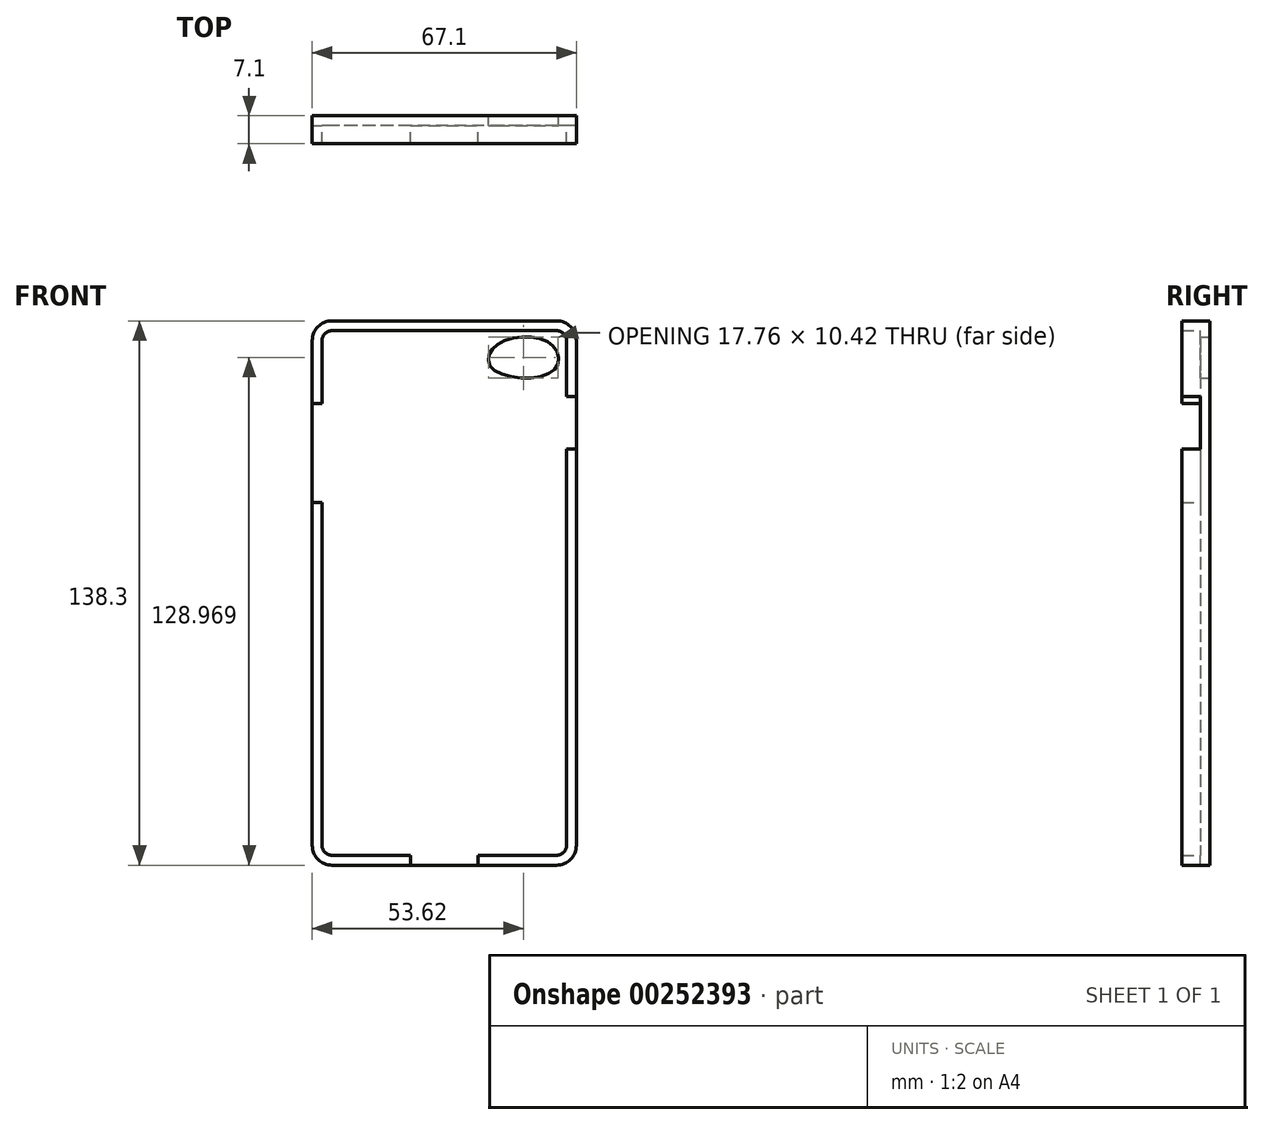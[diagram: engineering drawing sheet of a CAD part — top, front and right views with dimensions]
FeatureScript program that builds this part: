
annotation { "Feature Type Name" : "Feature", "Feature Type Description" : "" }
export const myFeature = defineFeature(function(context is Context, id is Id, definition is map)
    precondition{}
    {
        {
            var Q0;
            Q0=qCreatedBy(makeId("Front.planeOp"),FACE);
            var sketch = newSketch(context, id + "F0", { "sketchPlane" : qUnion([Q0])});
            skLineSegment(sketch, "E0.bottom", {"start": v(33.55, 69.15) * mm, "end": v(-33.55, 69.15) * mm});
            skLineSegment(sketch, "E0.top", {"start": v(33.55, -69.15) * mm, "end": v(-33.55, -69.15) * mm});
            skLineSegment(sketch, "E0.left", {"start": v(33.55, 69.15) * mm, "end": v(33.55, -69.15) * mm});
            skLineSegment(sketch, "E0.right", {"start": v(-33.55, 69.15) * mm, "end": v(-33.55, -69.15) * mm});
            skPoint(sketch, "E0.middle", {"position": v(0, 0) * mm});
            skSolve(sketch);
        }
        {
            var Q0;
            Q0=makeQuery(id+"F0.imprint","IMPRINT",FACE,{"disambiguationData":[TD([[makeQuery(id+"F0.imprint","IMPRINT",EDGE,{"derivedFrom":sQuery(id+"F0.wireOp",EDGE,"E0.bottom")}),1.0]])]});
            extrude(context, id + "F1", {"entities" : qUnion([Q0]), "endBound" : BoundingType.SYMMETRIC, "depth" : 7.1 * mm});
        }
        {
            var Q0;
            Q0=makeQuery(id+"F1.opExtrude","SWEPT_EDGE",EDGE,{"disambiguationData":[OSD([sQuery(id+"F0.wireOp",EDGE,"E0.bottom"),sQuery(id+"F0.wireOp",EDGE,"E0.right")])]});
            var Q1;
            Q1=makeQuery(id+"F1.opExtrude","SWEPT_EDGE",EDGE,{"disambiguationData":[OSD([sQuery(id+"F0.wireOp",EDGE,"E0.bottom"),sQuery(id+"F0.wireOp",EDGE,"E0.left")])]});
            var Q2;
            Q2=makeQuery(id+"F1.opExtrude","SWEPT_EDGE",EDGE,{"disambiguationData":[OSD([sQuery(id+"F0.wireOp",EDGE,"E0.top"),sQuery(id+"F0.wireOp",EDGE,"E0.right")])]});
            var Q3;
            Q3=makeQuery(id+"F1.opExtrude","SWEPT_EDGE",EDGE,{"disambiguationData":[OSD([sQuery(id+"F0.wireOp",EDGE,"E0.top"),sQuery(id+"F0.wireOp",EDGE,"E0.left")])]});
            fillet(context, id + "F2", {"entities" : qUnion([Q0, Q1, Q2, Q3]), "radius" : 5 * mm, "tangentPropagation" : true, "allowEdgeOverflow" : false});
        }
        {
            var Q0;
            Q0=makeQuery(id+"F1.opExtrude","CAP_FACE",FACE,{"disambiguationData":[OSD([sQuery(id+"F0.wireOp",EDGE,"E0.bottom"),sQuery(id+"F0.wireOp",EDGE,"E0.top"),sQuery(id+"F0.wireOp",EDGE,"E0.left"),sQuery(id+"F0.wireOp",EDGE,"E0.right")])],"isStart":false});
            shell(context, id + "F3", {"entities" : qUnion([Q0]), "thickness" : 2.5 * mm});
        }
        {
            var Q0;
            Q0=qCreatedBy(makeId("Front.planeOp"),FACE);
            var sketch = newSketch(context, id + "F4", { "sketchPlane" : qUnion([Q0])});
            skFitSpline(sketch, "E1", {"points": [v(13.55, 63.18) * mm, v(27.24, 63.18) * mm, v(27.47, 56.34) * mm, v(12.18, 57.02) * mm, v(13.55, 63.18) * mm]});
            skSolve(sketch);
        }
        {
            var Q0;
            Q0=makeQuery(id+"F4.imprint","IMPRINT",FACE,{"disambiguationData":[TD([[makeQuery(id+"F4.imprint","IMPRINT",EDGE,{"derivedFrom":sQuery(id+"F4.wireOp",EDGE,"E1")}),-1.0]])]});
            extrude(context, id + "F5", {"entities" : qUnion([Q0]), "operationType" : NewBodyOperationType.REMOVE, "endBound" : BoundingType.SYMMETRIC, "oppositeDirection" : true, "depth" : 25 * mm});
        }
        {
            var Q0;
            Q0=makeQuery(id+"F3.opShell","OFFSET_FACE",FACE,{"disambiguationData":[OSD([sQuery(id+"F0.wireOp",EDGE,"E0.top")])]});
            var sketch = newSketch(context, id + "F6", { "sketchPlane" : qUnion([Q0])});
            skLineSegment(sketch, "E2.bottom", {"start": v(-48.02, 129.36) * mm, "end": v(-44.8, 129.36) * mm});
            skLineSegment(sketch, "E2.top", {"start": v(-48.02, 126.28) * mm, "end": v(-44.8, 126.28) * mm});
            skLineSegment(sketch, "E2.left", {"start": v(-48.02, 129.36) * mm, "end": v(-48.02, 126.28) * mm});
            skLineSegment(sketch, "E2.right", {"start": v(-44.8, 129.36) * mm, "end": v(-44.8, 126.28) * mm});
            skPoint(sketch, "E2.middle", {"position": v(-46.4, 127.82) * mm});
            skLineSegment(sketch, "E3.bottom", {"start": v(8.6, 1.05) * mm, "end": v(-8.6, 1.05) * mm});
            skLineSegment(sketch, "E3.top", {"start": v(8.6, -4.96) * mm, "end": v(-8.6, -4.96) * mm});
            skLineSegment(sketch, "E3.left", {"start": v(8.6, 1.05) * mm, "end": v(8.6, -4.96) * mm});
            skLineSegment(sketch, "E3.right", {"start": v(-8.6, 1.05) * mm, "end": v(-8.6, -4.96) * mm});
            skPoint(sketch, "E3.middle", {"position": v(0, -1.95) * mm});
            skSolve(sketch);
        }
        {
            var Q0;
            {var subQ0=sQuery(id+"F6.wireOp",EDGE,"E3.bottom");Q0=makeQuery(id+"F6.imprint","IMPRINT",FACE,{"disambiguationData":[TD([[makeQuery(id+"F6.imprint","IMPRINT",EDGE,{"derivedFrom":subQ0}),1.0]])]});}
            extrude(context, id + "F7", {"entities" : qUnion([Q0]), "operationType" : NewBodyOperationType.REMOVE, "endBound" : BoundingType.SYMMETRIC, "oppositeDirection" : true, "depth" : 25 * mm});
        }
        {
            var Q0;
            Q0=makeQuery(id+"F3.opShell","OFFSET_FACE",FACE,{"disambiguationData":[OSD([sQuery(id+"F0.wireOp",EDGE,"E0.right")])]});
            var sketch = newSketch(context, id + "F8", { "sketchPlane" : qUnion([Q0])});
            skLineSegment(sketch, "E4.bottom", {"start": v(-3.55, 22.94) * mm, "end": v(1.05, 22.94) * mm});
            skLineSegment(sketch, "E4.top", {"start": v(-3.55, 48.11) * mm, "end": v(1.05, 48.11) * mm});
            skLineSegment(sketch, "E4.left", {"start": v(-3.55, 22.94) * mm, "end": v(-3.55, 48.11) * mm});
            skLineSegment(sketch, "E4.right", {"start": v(1.05, 22.94) * mm, "end": v(1.05, 48.11) * mm});
            skSolve(sketch);
        }
        {
            var Q0;
            Q0=makeQuery(id+"F8.imprint","IMPRINT",FACE,{"disambiguationData":[TD([[makeQuery(id+"F8.imprint","IMPRINT",EDGE,{"derivedFrom":sQuery(id+"F8.wireOp",EDGE,"E4.bottom")}),1.0]])]});
            extrude(context, id + "F9", {"entities" : qUnion([Q0]), "operationType" : NewBodyOperationType.REMOVE, "endBound" : BoundingType.SYMMETRIC, "oppositeDirection" : true, "depth" : 25 * mm});
        }
        {
            var Q0;
            Q0=makeQuery(id+"F3.opShell","OFFSET_FACE",FACE,{"disambiguationData":[OSD([sQuery(id+"F0.wireOp",EDGE,"E0.left")])]});
            var sketch = newSketch(context, id + "F10", { "sketchPlane" : qUnion([Q0])});
            skLineSegment(sketch, "E5.bottom", {"start": v(-1.05, 49.93) * mm, "end": v(3.55, 49.93) * mm});
            skLineSegment(sketch, "E5.top", {"start": v(-1.05, 36.53) * mm, "end": v(3.55, 36.53) * mm});
            skLineSegment(sketch, "E5.left", {"start": v(-1.05, 49.93) * mm, "end": v(-1.05, 36.53) * mm});
            skLineSegment(sketch, "E5.right", {"start": v(3.55, 49.93) * mm, "end": v(3.55, 36.53) * mm});
            skSolve(sketch);
        }
        {
            var Q0;
            Q0=makeQuery(id+"F10.imprint","IMPRINT",FACE,{"disambiguationData":[TD([[makeQuery(id+"F10.imprint","IMPRINT",EDGE,{"derivedFrom":sQuery(id+"F10.wireOp",EDGE,"E5.bottom")}),-1.0]])]});
            extrude(context, id + "F11", {"entities" : qUnion([Q0]), "operationType" : NewBodyOperationType.REMOVE, "endBound" : BoundingType.SYMMETRIC, "oppositeDirection" : true, "depth" : 25 * mm});
        }
    });
